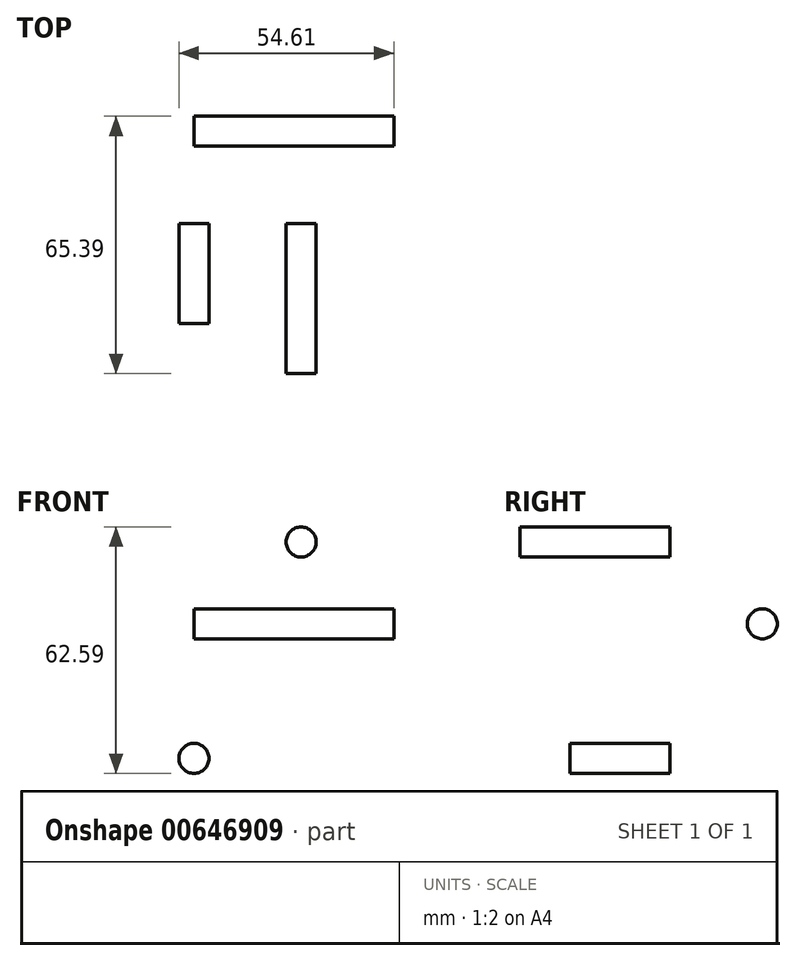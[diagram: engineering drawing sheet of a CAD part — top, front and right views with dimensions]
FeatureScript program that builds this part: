
annotation { "Feature Type Name" : "Feature", "Feature Type Description" : "" }
export const myFeature = defineFeature(function(context is Context, id is Id, definition is map)
    precondition{}
    {
        {
            var Q0;
            Q0=qCreatedBy(makeId("Front.planeOp"),FACE);
            var sketch = newSketch(context, id + "F0", { "sketchPlane" : qUnion([Q0])});
            skCircle(sketch, "E0", {"center": v(0, 0) * mm, "radius": 3.81 * mm});
            skSolve(sketch);
        }
        {
            var Q0;
            Q0 = qSketchRegion(id + "F0", true);
            extrude(context, id + "F1", {"entities" : qUnion([Q0]), "depth" : 25.4 * mm, "offsetDistance" : 25.4 * mm});
        }
        {
            var Q0;
            Q0=qCreatedBy(makeId("Front.planeOp"),FACE);
            var sketch = newSketch(context, id + "F2", { "sketchPlane" : qUnion([Q0])});
            skCircle(sketch, "E1", {"center": v(27.22, 54.97) * mm, "radius": 3.81 * mm});
            skSolve(sketch);
        }
        {
            var Q0;
            Q0 = qSketchRegion(id + "F2", true);
            extrude(context, id + "F3", {"entities" : qUnion([Q0]), "depth" : 38.1 * mm, "offsetDistance" : 25.4 * mm});
        }
        {
            var Q0;
            Q0=qCreatedBy(makeId("Right.planeOp"),FACE);
            var sketch = newSketch(context, id + "F4", { "sketchPlane" : qUnion([Q0])});
            skCircle(sketch, "E2", {"center": v(23.48, 34.19) * mm, "radius": 3.81 * mm});
            skSolve(sketch);
        }
        {
            var Q0;
            Q0 = qSketchRegion(id + "F4", true);
            extrude(context, id + "F5", {"entities" : qUnion([Q0]), "depth" : 50.8 * mm, "offsetDistance" : 25.4 * mm});
        }
    });
